# Revit family: SEA SERIES
name_source: partatom
category: Communication Devices
revit_build: Autodesk Revit 2014 (Build: 20140709_2115(x64)
units: mm (PartAtom-declared; Revit-internal decimal feet)

## types (2) — shared parameters
Body Material = QF_Plastic - White - Smooth
Color = QF_Plastic - White - Smooth
Enclosure Material = QF_Rubber - Black - Smooth
Family Code (default) = LOUD SPEAKER ENCLOSURES
Family Version = 2017-01
Height = 5 "
IQ Category = AUDIO VISUAL ENCLOSURES
Identify Quantity as Lot = Yes
Manufacturer = ATLAS SOUND
Manufacturer URL = https://www.atlasied.com
MasterFormat = 27 42 19
MaterFormat Title = AUDIO VISUAL ENCLOSURES
Mount Material = QF_Rubber - Black - Smooth
OmniClass Number = 23-37 27 15 13
OmniClass Title = AUDIO VISUAL ENCLOSURES
Product Documentation Link = https://www.atlasied.com
Regulatory Compliance = UL Listed, 70V/100V Capable
URL = https://www.atlasied.com
Warranty = 1 Year
zero-valued in all types: Cost, Cost MSRP

## per-type parameters (varying)
| type | Bottom Dimension | Depth | Description | Model | Product Page URL | Width |
| SEA-18S | 3 " | 11.71 " | SLANTED SURFACE MOUNT ENCLOSURE IS DESIGNED FOR USE ONLY WITH ATLAS SOUND LOUDSPEAKER SYSTEM MODELS I8S AND I8SM. THE SLOPE FRONT DESIGN ALLOWS FOR DIRECTIONAL SOUND DISPERSION. THE ENCLOSURE IS CONSTRUCTED OF 20-GAUGE CRS AND FINISHED IN TEXTURED WHITE EPOXY. | SEA-I8S | https://www.atlasied.com | 11.75 " |
| SEA-18SC | 2.5 " | 14.41 " | STRAIGHT SURFACE MOUNT ENCLOSURE IS DESIGNED FOR USE ONLY WITH ATLAS SOUND LOUDSPEAKER SYSTEM MODELS I8SC AND I8SCM. THE UNIT PROVIDES AN ARCHITECTURALLY PLEASING APPEARANCE WITH CRISP LINES THAT BLEND WELL WITH MOST BUILDING INTERIORS. THE ENCLOSURE IS CONSTRUCTED OF 20-GAUGE CRS AND FINISHED IN RECLAIMED POWDER COAT FINISH.FEST-I8SCFLUSH MOUNT ENCLOSURE IS DESIGNED FOR USE ONLY WITH ATLAS SOUND LOUDSPEAKER SYSTEM MODELS I8SC, I8SCH, AND I8SCM. THE UNIT INCLUDES A SLOT STYLE MOUNTING SYSTEM TO ACCOMMODATE MOST ANY MATERIAL THICKNESS. THE ENCLOSURE IS CONSTRUCTED OF 20-GAUGE CRS AND FINISHED IN TEXTURED WHITE EPOXY.SEST-IHSTRAIGHT SURFACE MOUNT STAINLESS STEEL ENCLOSURE IS DESIGNED FOR USE ONLY WITH ATLAS SOUND LOUDSPEAKER SYSTEM MODEL IHVP. THE ENCLOSURE IS CONSTRUCTED OF 18-GAUGE STAINLESS STEEL AND FINISHED IN TEXTURED WHITE EPOXY.FEST-IHFLUSH MOUNT STAINLESS STEEL ENCLOSURE IS DESIGNED FOR USE ONLY WITH ATLAS SOUND LOUDSPEAKER SYSTEM MODEL IHVP. EXTERNAL MOUNTING WINGS ALLOW FOR EASY INSTALLATION INTO STUD MATERIAL. THE ENCLOSURE IS CONSTRUCTED OF 18-GAUGE STAINLESS STEEL. SEA SERIESSEST SERIESFEST SERIES | SEA-I8SC | https://www.atlasied.com
https://www.atlasied.com
https://www.atlasied.com
https://www.atlasied.com
https://www.atlasied.com | 13 " |

## geometry (parser evidence)
native form markers: Sweep x5
no freeform markers — native parametric forms only
